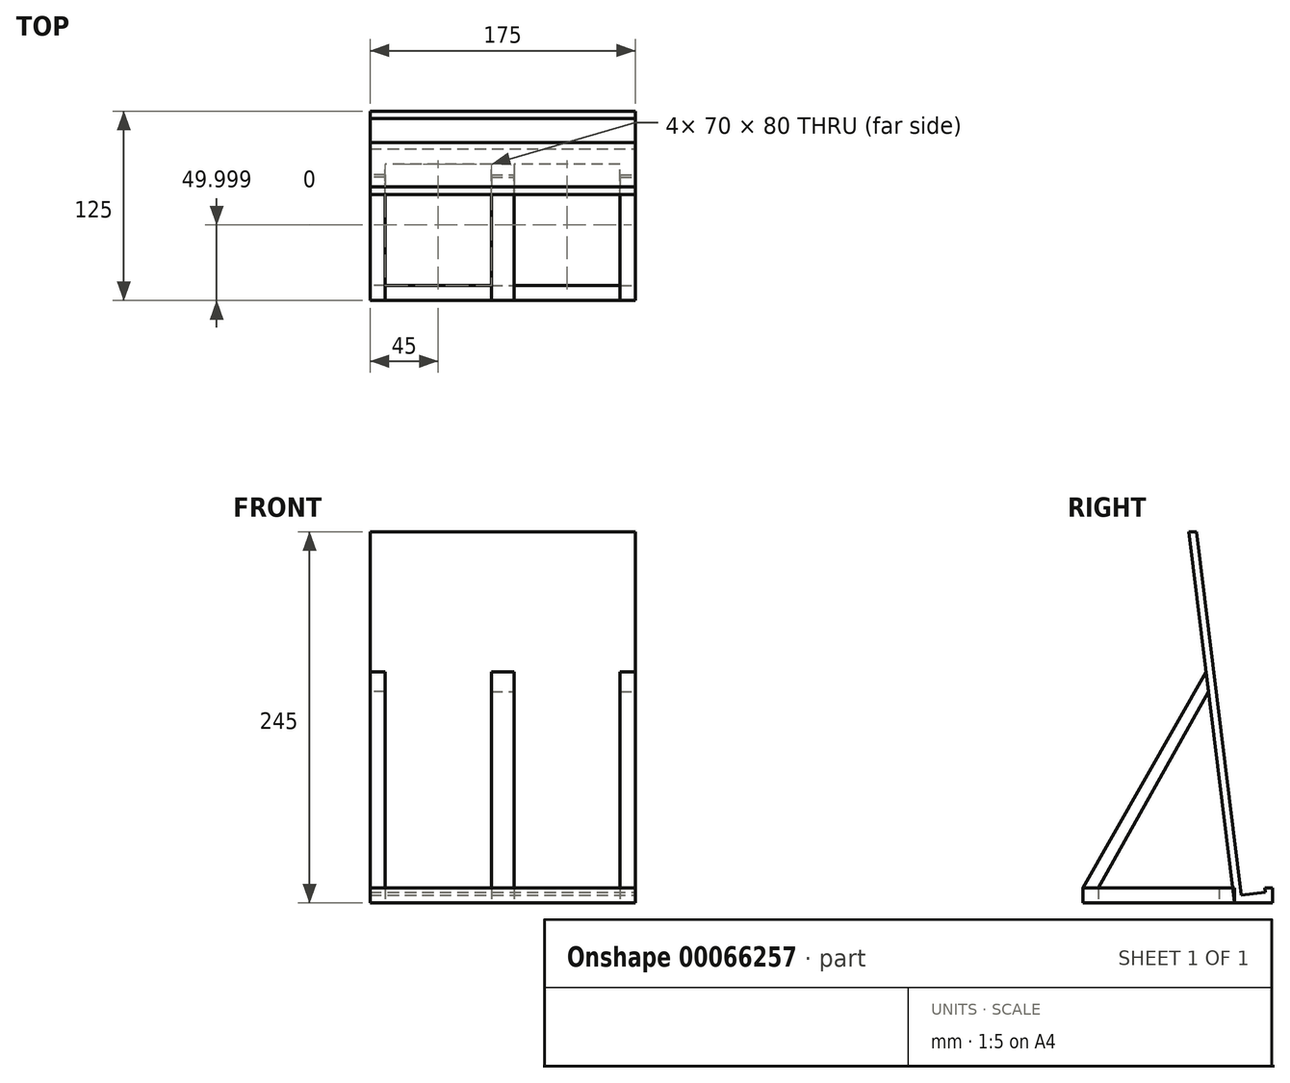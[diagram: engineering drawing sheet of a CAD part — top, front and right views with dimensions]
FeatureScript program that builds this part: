
annotation { "Feature Type Name" : "Feature", "Feature Type Description" : "" }
export const myFeature = defineFeature(function(context is Context, id is Id, definition is map)
    precondition{}
    {
        {
            var Q0;
            Q0=qCreatedBy(makeId("Right.planeOp"),FACE);
            var sketch = newSketch(context, id + "F0", { "sketchPlane" : qUnion([Q0])});
            skLineSegment(sketch, "E0", {"start": v(-110.08, -6.95) * mm, "end": v(-85.08, -6.95) * mm});
            skLineSegment(sketch, "E1", {"start": v(-105.7, -1.89) * mm, "end": v(-135.08, 238.05) * mm});
            skLineSegment(sketch, "E2", {"start": v(-85.08, -6.95) * mm, "end": v(-85.08, 3.05) * mm});
            skLineSegment(sketch, "E3", {"start": v(-85.08, 3.05) * mm, "end": v(-90.08, 3.05) * mm});
            skLineSegment(sketch, "E4", {"start": v(-90.08, 3.05) * mm, "end": v(-89.72, 0.07) * mm});
            skLineSegment(sketch, "E5", {"start": v(-89.72, 0.07) * mm, "end": v(-105.7, -1.89) * mm});
            skPoint(sketch, "E6.orphan", {"position": v(-105.08, -6.95) * mm});
            skLineSegment(sketch, "E7", {"start": v(-135.08, 238.05) * mm, "end": v(-140.08, 238.05) * mm});
            skLineSegment(sketch, "E8", {"start": v(-140.08, 238.05) * mm, "end": v(-110.08, -6.95) * mm});
            skSolve(sketch);
        }
        {
            var Q0;
            Q0=makeQuery(id+"F0.imprint","IMPRINT",FACE,{"disambiguationData":[TD([[makeQuery(id+"F0.imprint","IMPRINT",EDGE,{"derivedFrom":sQuery(id+"F0.wireOp",EDGE,"E0")}),1.0]])]});
            extrude(context, id + "F1", {"entities" : qUnion([Q0]), "oppositeDirection" : true, "depth" : 175 * mm, "offsetDistance" : 25 * mm});
        }
        {
            var Q0;
            Q0=makeQuery(id+"F1.opExtrude","SWEPT_FACE",FACE,{"disambiguationData":[OSD([sQuery(id+"F0.wireOp",EDGE,"E0")])]});
            var sketch = newSketch(context, id + "F2", { "sketchPlane" : qUnion([Q0])});
            skLineSegment(sketch, "E9", {"start": v(0, 110.08) * mm, "end": v(-175, 110.08) * mm});
            skLineSegment(sketch, "E10", {"start": v(-175, 110.08) * mm, "end": v(-175, 210.08) * mm});
            skLineSegment(sketch, "E11", {"start": v(0, 110.08) * mm, "end": v(0, 210.08) * mm});
            skLineSegment(sketch, "E12", {"start": v(0, 210.08) * mm, "end": v(-175, 210.08) * mm});
            skLineSegment(sketch, "E13.bottom", {"start": v(-10, 200.08) * mm, "end": v(-80, 200.08) * mm});
            skLineSegment(sketch, "E13.top", {"start": v(-10, 120.08) * mm, "end": v(-80, 120.08) * mm});
            skLineSegment(sketch, "E13.left", {"start": v(-10, 200.08) * mm, "end": v(-10, 120.08) * mm});
            skLineSegment(sketch, "E13.right", {"start": v(-165, 200.08) * mm, "end": v(-165, 120.08) * mm});
            skLineSegment(sketch, "E14", {"start": v(-80, 120.08) * mm, "end": v(-80, 200.08) * mm});
            skLineSegment(sketch, "E15", {"start": v(-95, 200.08) * mm, "end": v(-95, 120.08) * mm});
            skLineSegment(sketch, "E16.trimOffspring", {"start": v(-95, 200.08) * mm, "end": v(-165, 200.08) * mm});
            skLineSegment(sketch, "E17.trimOffspring", {"start": v(-95, 120.08) * mm, "end": v(-165, 120.08) * mm});
            skSolve(sketch);
        }
        {
            var Q0;
            Q0=makeQuery(id+"F2.imprint","IMPRINT",FACE,{"disambiguationData":[TD([[makeQuery(id+"F2.imprint","IMPRINT",EDGE,{"derivedFrom":sQuery(id+"F2.wireOp",EDGE,"E9")}),1.0]])]});
            extrude(context, id + "F3", {"entities" : qUnion([Q0]), "oppositeDirection" : true, "depth" : 10 * mm, "offsetDistance" : 25 * mm});
        }
        {
            var Q0;
            Q0=makeQuery(id+"F3.opExtrude","SWEPT_FACE",FACE,{"disambiguationData":[OSD([sQuery(id+"F2.wireOp",EDGE,"E10")])]});
            var sketch = newSketch(context, id + "F4", { "sketchPlane" : qUnion([Q0])});
            skLineSegment(sketch, "E18.0.0", {"start": v(135.08, 238.05) * mm, "end": v(105.7, -1.89) * mm});
            skLineSegment(sketch, "E18.0.1", {"start": v(105.7, -1.89) * mm, "end": v(89.72, 0.07) * mm});
            skLineSegment(sketch, "E18.0.2", {"start": v(89.72, 0.07) * mm, "end": v(90.08, 3.05) * mm});
            skLineSegment(sketch, "E18.0.3", {"start": v(90.08, 3.05) * mm, "end": v(85.08, 3.05) * mm});
            skLineSegment(sketch, "E18.0.4", {"start": v(85.08, 3.05) * mm, "end": v(85.08, -6.95) * mm});
            skLineSegment(sketch, "E18.0.5", {"start": v(85.08, -6.95) * mm, "end": v(110.08, -6.95) * mm});
            skLineSegment(sketch, "E18.0.6", {"start": v(110.08, -6.95) * mm, "end": v(140.08, 238.05) * mm});
            skLineSegment(sketch, "E18.0.7", {"start": v(140.08, 238.05) * mm, "end": v(135.08, 238.05) * mm});
            skLineSegment(sketch, "E19", {"start": v(210.08, 3.05) * mm, "end": v(128.76, 145.6) * mm});
            skLineSegment(sketch, "E20", {"start": v(127.18, 132.68) * mm, "end": v(200.08, 3.05) * mm});
            skSolve(sketch);
        }
        {
            var Q0;
            {var subQ0=sQuery(id+"F4.wireOp",EDGE,"E19");Q0=makeQuery(id+"F4.imprint","IMPRINT",FACE,{"disambiguationData":[TD([[makeQuery(id+"F4.imprint","IMPRINT",EDGE,{"derivedFrom":subQ0}),1.0]])]});}
            extrude(context, id + "F5", {"entities" : qUnion([Q0]), "oppositeDirection" : true, "depth" : 10 * mm, "offsetDistance" : 25 * mm});
        }
        {
            var Q0;
            Q0=makeQuery(id+"F3.opExtrude","SWEPT_FACE",FACE,{"disambiguationData":[OSD([sQuery(id+"F2.wireOp",EDGE,"E11")])]});
            var sketch = newSketch(context, id + "F6", { "sketchPlane" : qUnion([Q0])});
            skLineSegment(sketch, "E21.0.0", {"start": v(-127.18, 132.68) * mm, "end": v(-128.76, 145.6) * mm});
            skLineSegment(sketch, "E21.0.1", {"start": v(-128.76, 145.6) * mm, "end": v(-210.08, 3.05) * mm});
            skLineSegment(sketch, "E21.0.2", {"start": v(-210.08, 3.05) * mm, "end": v(-200.08, 3.05) * mm});
            skLineSegment(sketch, "E21.0.3", {"start": v(-200.08, 3.05) * mm, "end": v(-127.18, 132.68) * mm});
            skSolve(sketch);
        }
        {
            var Q0;
            Q0 = qSketchRegion(id + "F6", true);
            extrude(context, id + "F7", {"entities" : qUnion([Q0]), "oppositeDirection" : true, "depth" : 10 * mm, "offsetDistance" : 25 * mm});
        }
        {
            var Q0;
            Q0=makeQuery(id+"F3.opExtrude","SWEPT_FACE",FACE,{"disambiguationData":[OSD([sQuery(id+"F2.wireOp",EDGE,"E14")])]});
            var sketch = newSketch(context, id + "F8", { "sketchPlane" : qUnion([Q0])});
            skLineSegment(sketch, "E22.0.0", {"start": v(-127.18, 132.68) * mm, "end": v(-128.76, 145.6) * mm});
            skLineSegment(sketch, "E22.0.1", {"start": v(-128.76, 145.6) * mm, "end": v(-210.08, 3.05) * mm});
            skLineSegment(sketch, "E22.0.2", {"start": v(-210.08, 3.05) * mm, "end": v(-200.08, 3.05) * mm});
            skLineSegment(sketch, "E22.0.3", {"start": v(-200.08, 3.05) * mm, "end": v(-127.18, 132.68) * mm});
            skSolve(sketch);
        }
        {
            var Q0;
            Q0 = qSketchRegion(id + "F8", true);
            var Q1;
            Q1=makeQuery(id+"F3.opExtrude","SWEPT_FACE",FACE,{"disambiguationData":[OSD([sQuery(id+"F2.wireOp",EDGE,"E15")])]});
            extrude(context, id + "F9", {"entities" : qUnion([Q0]), "endBound" : BoundingType.UP_TO_SURFACE, "oppositeDirection" : true, "depth" : 10 * mm, "endBoundEntityFace" : qUnion([Q1]), "offsetDistance" : 25 * mm});
        }
    });
